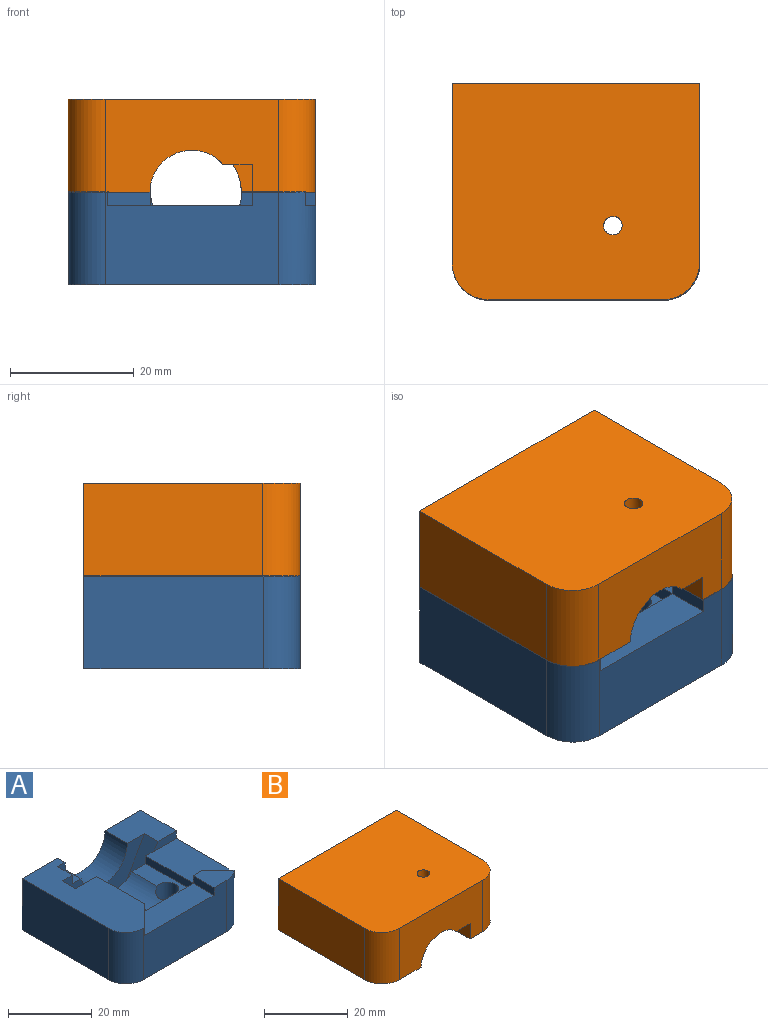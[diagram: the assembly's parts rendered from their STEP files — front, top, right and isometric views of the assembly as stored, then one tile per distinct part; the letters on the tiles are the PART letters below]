
ASSEMBLY  parts=2 mates=1
PART A: 36 faces, bbox 40x35x15 mm
  f0: plane 35x13.25mm, normal (0,0,1), area 377.7mm2, adj f1,f6,f7,f8,f10,f13,f14,f24
  f1: plane 27.71x12mm, normal (0,-1,0), area 142.3mm2, adj f0,f4,f10,f11,f12,f24,f25,f27
  f2: plane 8.49x7mm, normal (0,0,1), area 43.4mm2, adj f3,f8,f20,f29,f30
  f3: plane 3.25x2.25mm, normal (0,1,0), area 7.3mm2, adj f2,f17,f20,f29
  f4: plane 12x12mm, normal (0,0,1), area 117.6mm2, adj f1,f5,f6,f12,f19,f24
  f5: plane 29x15mm, normal (1,0,0), area 396.8mm2, adj f4,f6,f9,f17,f19,f30
  f6: plane 40x15mm, normal (0,1,0), area 485.3mm2, adj f0,f4,f5,f7,f9,f24,f32,f34
  f7: plane 29x15mm, normal (-1,0,0), area 435mm2, adj f0,f6,f9,f31
  f8: plane 28x15mm, normal (0,-1,0), area 367.1mm2, adj f0,f2,f9,f20,f22,f28,f30,f31
  f9: plane 40x35mm, normal (0,0,-1), area 1360.8mm2, adj f5,f6,f7,f8,f23,f30,f31
  f10: plane 12x6.93mm, normal (0.87,0,0.5), area 62.4mm2, adj f0,f1,f11,f13
  f11: plane 13.86x4.5mm, normal (0,0,1), area 62.4mm2, adj f1,f10,f12,f13
  f12: plane 12x6.93mm, normal (-0.87,0,0.5), area 62.4mm2, adj f1,f4,f11,f13,f19
  f13: plane 26.41x12mm, normal (0,1,0), area 154.1mm2, adj f0,f10,f11,f12,f14,f15,f16,f17
  f14: cylinder r=6.75mm len=16mm, axis (0,1,0), area 251.7mm2, adj f0,f13,f15,f18,f21,f23
  f15: plane 16x4.72mm, normal (0,0,1), area 58.4mm2, adj f13,f14,f16,f18,f23
  f16: plane 16x2.25mm, normal (-1,0,0), area 36mm2, adj f13,f15,f17,f18
  f17: plane 21.24x10.25mm, normal (0,0,1), area 184.6mm2, adj f3,f5,f13,f16,f19,f29,f30
  f18: plane 16.11x4.5mm, normal (0,1,0), area 50.7mm2, adj f14,f15,f16,f22
  f19: plane 7.44x2.25mm, normal (0,-1,0), area 15.3mm2, adj f4,f5,f12,f17
  f20: plane 7x2.25mm, normal (-1,0,0), area 15.8mm2, adj f2,f3,f8,f22
  f21: plane 2.25x0.39mm, normal (0,-1,0), area 0.3mm2, adj f14,f22,f28
  f22: plane 23.5x7mm, normal (0,0,1), area 140mm2, adj f8,f18,f20,f21,f28
  f23: cylinder r=2.75mm len=10.5mm, axis (0,0,1), area 174.9mm2, adj f9,f14,f15
  f24: cylinder r=8mm len=16mm, axis (0,1,0), area 175.8mm2, adj f0,f1,f4,f6,f26,f27
  f25: plane 5x2.5mm, normal (1,0,0), area 12.5mm2, adj f0,f1,f26,f27
  f26: plane 2.9x2.5mm, normal (0,-1,0), area 6.6mm2, adj f0,f24,f25,f27
  f27: plane 5x2.9mm, normal (0,0,1), area 14.5mm2, adj f1,f24,f25,f26
  f28: plane 7x7mm, normal (0.71,-0.71,0), area 22.3mm2, adj f0,f8,f21,f22
  f29: plane 5.24x5.24mm, normal (0.71,0.71,0), area 16.7mm2, adj f2,f3,f17,f30
  f30: cylinder r=6mm len=15mm, axis (0,0,1), area 130.8mm2, adj f2,f5,f8,f9,f17,f29
  f31: cylinder r=6mm len=15mm, axis (0,0,-1), area 141.4mm2, adj f0,f7,f8,f9
  f32: cylinder r=1.5mm len=25mm, axis (0,1,0), area 235.6mm2, adj f6,f33
  f33: plane 3x3mm, normal (0,1,0), area 7.1mm2, adj f32
  f34: cylinder r=1.5mm len=25mm, axis (0,1,0), area 235.6mm2, adj f6,f35
  f35: plane 3x3mm, normal (0,1,0), area 7.1mm2, adj f34
PART B: 30 faces, bbox 40x35x15 mm
  f0: plane 16x10.25mm, normal (0,0,-1), area 164mm2, adj f9,f11,f15,f17,f22
  f1: plane 35x13.25mm, normal (0,0,-1), area 402.2mm2, adj f2,f3,f6,f7,f8,f11,f14,f16
  f2: cylinder r=8mm len=16mm, axis (0,1,0), area 182.2mm2, adj f1,f3,f5,f6,f20,f21
  f3: plane 27.71x12mm, normal (0,-1,0), area 145.7mm2, adj f1,f2,f5,f12,f13,f14,f19,f21
  f4: cylinder r=1.5mm len=10.5mm, axis (0,0,-1), area 98mm2, adj f10,f16,f18
  f5: plane 12x12mm, normal (0,0,-1), area 117.6mm2, adj f2,f3,f6,f9,f12,f15
  f6: plane 40x15mm, normal (0,1,0), area 485.3mm2, adj f1,f2,f5,f7,f9,f10,f26,f28
  f7: plane 29x15mm, normal (-1,0,0), area 435mm2, adj f1,f6,f10,f24
  f8: plane 28x15mm, normal (0,-1,0), area 332.5mm2, adj f1,f10,f16,f17,f18,f23,f24,f25
  f9: plane 29x15mm, normal (1,0,0), area 399mm2, adj f0,f5,f6,f10,f15,f22,f23,f25
  f10: plane 40x35mm, normal (0,0,1), area 1377.5mm2, adj f4,f6,f7,f8,f9,f24,f25
  f11: plane 26.41x12mm, normal (0,1,0), area 154.1mm2, adj f0,f1,f12,f13,f14,f16,f17,f18
  f12: plane 12x6.93mm, normal (-0.87,0,-0.5), area 62.4mm2, adj f3,f5,f11,f13,f15
  f13: plane 13.86x4.5mm, normal (0,0,-1), area 62.4mm2, adj f3,f11,f12,f14
  f14: plane 12x6.93mm, normal (0.87,0,-0.5), area 62.4mm2, adj f1,f3,f11,f13
  f15: plane 7.44x2.25mm, normal (0,-1,0), area 15.3mm2, adj f0,f5,f9,f12
  f16: cylinder r=6.75mm len=23mm, axis (0,-1,0), area 373.2mm2, adj f1,f4,f8,f11,f18
  f17: plane 23x4.5mm, normal (-1,0,0), area 67.5mm2, adj f0,f8,f11,f18,f22,f23
  f18: plane 23x4.72mm, normal (0,0,-1), area 102.3mm2, adj f4,f8,f11,f16,f17
  f19: plane 5x1.25mm, normal (1,0,0), area 6.3mm2, adj f1,f3,f20,f21
  f20: plane 2.6x1.25mm, normal (0,-1,0), area 3.2mm2, adj f1,f2,f19,f21
  f21: plane 5x2.6mm, normal (0,0,-1), area 13mm2, adj f2,f3,f19,f20
  f22: plane 10.25x2.25mm, normal (0,1,0), area 23.1mm2, adj f0,f9,f17,f23
  f23: plane 10.25x7mm, normal (0,0,-1), area 64mm2, adj f8,f9,f17,f22,f25
  f24: cylinder r=6mm len=15mm, axis (0,0,-1), area 141.4mm2, adj f1,f7,f8,f10
  f25: cylinder r=6mm len=15mm, axis (0,0,1), area 141.4mm2, adj f8,f9,f10,f23
  f26: cylinder r=1.5mm len=25mm, axis (0,1,0), area 235.6mm2, adj f6,f27
  f27: plane 3x3mm, normal (0,1,0), area 7.1mm2, adj f26
  f28: cylinder r=1.5mm len=25mm, axis (0,1,0), area 235.6mm2, adj f6,f29
  f29: plane 3x3mm, normal (0,1,0), area 7.1mm2, adj f28
PLACE A t=(0.1,-0.28,0)mm
PLACE B t=(0.03,-0.21,-1)mm
MATE slider A.f9 <-> B.f10  axis (0,0,-1) through (0,0,0)mm
